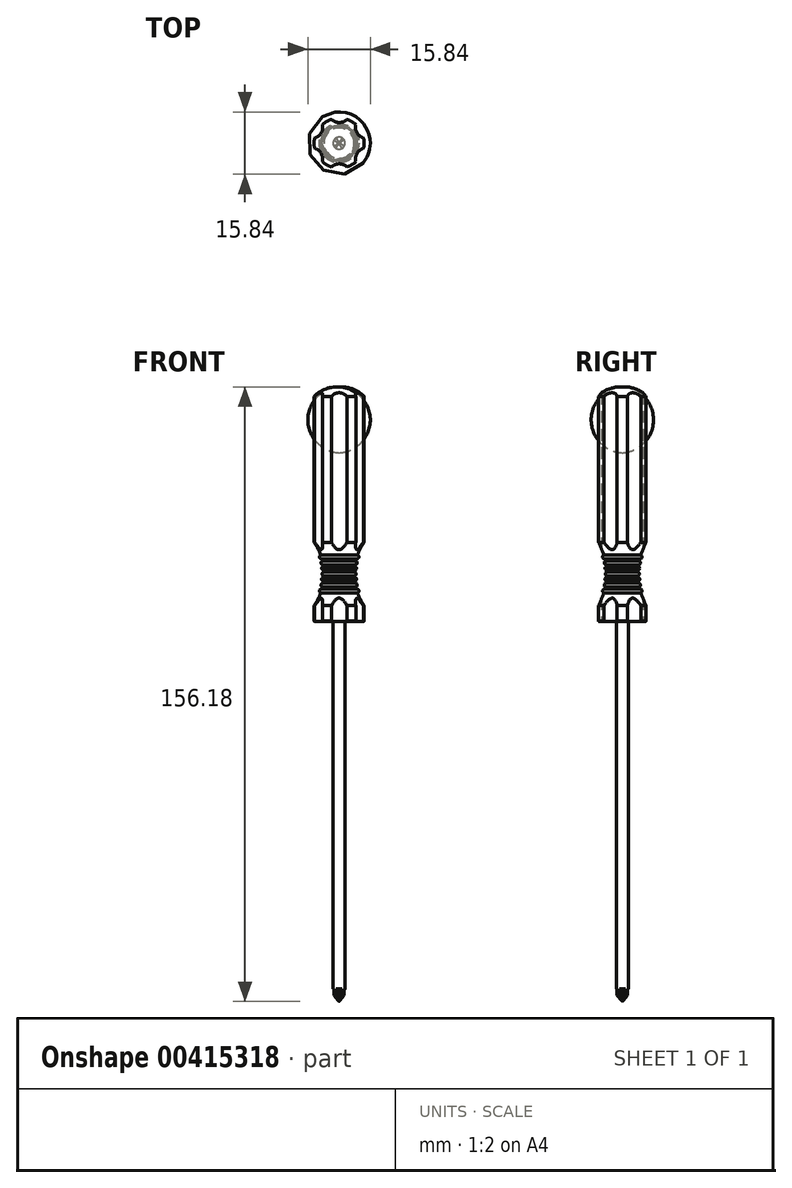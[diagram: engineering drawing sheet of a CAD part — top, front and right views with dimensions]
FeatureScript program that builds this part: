
annotation { "Feature Type Name" : "Feature", "Feature Type Description" : "" }
export const myFeature = defineFeature(function(context is Context, id is Id, definition is map)
    precondition{}
    {
        {
            var Q0;
            Q0=qCreatedBy(makeId("Front.planeOp"),FACE);
            var sketch = newSketch(context, id + "F0", { "sketchPlane" : qUnion([Q0])});
            skLineSegment(sketch, "E0", {"start": v(-6.35, 0) * mm, "end": v(-6.35, 57.15) * mm});
            skArc(sketch, "E1", {"start": v(0, 59.55) * mm, "mid": v(-3.43, 59.02) * mm, "end": v(-6.35, 57.15) * mm});
            skLineSegment(sketch, "E2", {"start": v(-6.35, 0) * mm, "end": v(-1.52, 0) * mm});
            skLineSegment(sketch, "E3", {"start": v(-1.52, 0) * mm, "end": v(-1.52, -95.1) * mm});
            skLineSegment(sketch, "E4", {"start": v(-1.52, -95.1) * mm, "end": v(0, -96.62) * mm});
            skLineSegment(sketch, "E5", {"start": v(0, -96.62) * mm, "end": v(0, 0) * mm});
            skPoint(sketch, "E6.end.orphan", {"position": v(0, 57.8) * mm});
            skLineSegment(sketch, "E7", {"start": v(0, 0) * mm, "end": v(0, 59.55) * mm});
            skSolve(sketch);
        }
        {
            var Q0;
            Q0 = qSketchRegion(id + "F0", true);
            var Q1;
            Q1=sQuery(id+"F0.wireOp",EDGE,"E7");
            revolve(context, id + "F1", {"entities" : qUnion([Q0]), "axis" : qUnion([Q1]), "revolveType" : RevolveType.FULL});
        }
        {
            var Q0;
            Q0=qCreatedBy(makeId("Front.planeOp"),FACE);
            var sketch = newSketch(context, id + "F2", { "sketchPlane" : qUnion([Q0])});
            skLineSegment(sketch, "E8", {"start": v(0, 0) * mm, "end": v(0, 87.28) * mm, "construction": true});
            skLineSegment(sketch, "E9", {"start": v(-6.93, 20.86) * mm, "end": v(-17.62, 12.03) * mm});
            skLineSegment(sketch, "E10", {"start": v(-17.62, 12.03) * mm, "end": v(-6.93, 3.2) * mm});
            skLineSegment(sketch, "E11", {"start": v(-6.93, 0.53) * mm, "end": v(-5.13, -0.97) * mm});
            skLineSegment(sketch, "E12", {"start": v(-5.13, -0.97) * mm, "end": v(-6.93, -0.97) * mm});
            skLineSegment(sketch, "E13", {"start": v(-6.93, -0.97) * mm, "end": v(-6.93, 0.53) * mm});
            skArc(sketch, "E14", {"start": v(-6.93, 3.2) * mm, "mid": v(-6.17, 4.25) * mm, "end": v(-5.51, 5.36) * mm});
            skArc(sketch, "E15", {"start": v(-4.67, 16.82) * mm, "mid": v(-5, 16.2) * mm, "end": v(-4.37, 15.89) * mm});
            skArc(sketch, "E16", {"start": v(-4.23, 15.33) * mm, "mid": v(-4.6, 14.76) * mm, "end": v(-4.03, 14.38) * mm});
            skArc(sketch, "E17.trimOffspring", {"start": v(-5.51, 18.7) * mm, "mid": v(-6.17, 19.82) * mm, "end": v(-6.93, 20.86) * mm});
            skArc(sketch, "E18.trimOffspring", {"start": v(-4.87, 17.34) * mm, "mid": v(-5.18, 18.03) * mm, "end": v(-5.51, 18.7) * mm});
            skArc(sketch, "E19.trimOffspring", {"start": v(-4.67, 16.82) * mm, "mid": v(-4.77, 17.08) * mm, "end": v(-4.87, 17.34) * mm});
            skArc(sketch, "E20.trimOffspring", {"start": v(-4.23, 15.33) * mm, "mid": v(-4.3, 15.61) * mm, "end": v(-4.37, 15.89) * mm});
            skLineSegment(sketch, "E21", {"start": v(-17.62, 12.03) * mm, "end": v(10.97, 12.03) * mm, "construction": true});
            skArc(sketch, "E22.MirrorCS", {"start": v(-4.67, 7.25) * mm, "mid": v(-4.77, 6.98) * mm, "end": v(-4.87, 6.72) * mm});
            skArc(sketch, "E23.MirrorCS", {"start": v(-4.23, 8.73) * mm, "mid": v(-4.3, 8.46) * mm, "end": v(-4.37, 8.18) * mm});
            skArc(sketch, "E24.MirrorCS", {"start": v(-5.27, 5.83) * mm, "mid": v(-5.4, 5.6) * mm, "end": v(-5.51, 5.36) * mm});
            skArc(sketch, "E25.MirrorCS", {"start": v(-4.67, 7.25) * mm, "mid": v(-5, 7.87) * mm, "end": v(-4.37, 8.18) * mm});
            skArc(sketch, "E26.MirrorCS", {"start": v(-4.23, 8.73) * mm, "mid": v(-4.6, 9.3) * mm, "end": v(-4.03, 9.7) * mm});
            skArc(sketch, "E27.trimOffspring", {"start": v(-4.03, 9.7) * mm, "mid": v(-4, 9.95) * mm, "end": v(-3.96, 10.2) * mm});
            skArc(sketch, "E28.trimOffspring", {"start": v(-4.37, 8.18) * mm, "mid": v(-4.3, 8.46) * mm, "end": v(-4.23, 8.73) * mm});
            skArc(sketch, "E29.trimOffspring", {"start": v(-4.87, 6.72) * mm, "mid": v(-4.77, 6.98) * mm, "end": v(-4.67, 7.25) * mm});
            skArc(sketch, "E30.trimOffspring", {"start": v(-5.51, 5.36) * mm, "mid": v(-5.18, 6.03) * mm, "end": v(-4.87, 6.72) * mm});
            skArc(sketch, "E31", {"start": v(-3.85, 12.52) * mm, "mid": v(-4.33, 12.03) * mm, "end": v(-3.85, 11.55) * mm});
            skArc(sketch, "E32", {"start": v(-3.87, 11.17) * mm, "mid": v(-4.43, 10.74) * mm, "end": v(-3.96, 10.2) * mm});
            skArc(sketch, "E33", {"start": v(-3.97, 13.96) * mm, "mid": v(-4.4, 13.42) * mm, "end": v(-3.87, 12.99) * mm});
            skArc(sketch, "E34.trimOffspring", {"start": v(-3.97, 13.96) * mm, "mid": v(-4, 14.17) * mm, "end": v(-4.03, 14.38) * mm});
            skArc(sketch, "E35.trimOffspring", {"start": v(-3.85, 12.52) * mm, "mid": v(-3.86, 12.75) * mm, "end": v(-3.87, 12.99) * mm});
            skArc(sketch, "E36.trimOffspring", {"start": v(-3.87, 11.17) * mm, "mid": v(-3.86, 11.36) * mm, "end": v(-3.85, 11.55) * mm});
            skPoint(sketch, "E37.orphan", {"position": v(-6, 19.55) * mm});
            skPoint(sketch, "E38.orphan", {"position": v(-5.27, 18.24) * mm});
            skSolve(sketch);
        }
        {
            var Q0;
            Q0 = qSketchRegion(id + "F2", true);
            var Q1;
            Q1=sQuery(id+"F2.wireOp",EDGE,"E8");
            revolve(context, id + "F3", {"operationType" : NewBodyOperationType.REMOVE, "entities" : qUnion([Q0]), "axis" : qUnion([Q1]), "revolveType" : RevolveType.FULL, "oppositeDirection" : true});
        }
        {
            var Q0;
            Q0=qCreatedBy(makeId("Top.planeOp"),FACE);
            var sketch = newSketch(context, id + "F4", { "sketchPlane" : qUnion([Q0])});
            skArc(sketch, "E39", {"start": v(-2, 6.04) * mm, "mid": v(0, 5.25) * mm, "end": v(2, 6.04) * mm});
            skLineSegment(sketch, "E40", {"start": v(-2, 6.04) * mm, "end": v(0, 8.15) * mm});
            skLineSegment(sketch, "E41", {"start": v(2, 6.04) * mm, "end": v(0, 8.15) * mm});
            skArc(sketch, "E42.1.0", {"start": v(-6.23, 1.3) * mm, "mid": v(-4.55, 2.63) * mm, "end": v(-4.24, 4.74) * mm});
            skLineSegment(sketch, "E42.1.1", {"start": v(-6.23, 1.3) * mm, "end": v(-7.06, 4.08) * mm});
            skLineSegment(sketch, "E42.1.2", {"start": v(-4.24, 4.74) * mm, "end": v(-7.06, 4.08) * mm});
            skArc(sketch, "E42.2.0", {"start": v(-4.24, -4.74) * mm, "mid": v(-4.55, -2.63) * mm, "end": v(-6.23, -1.3) * mm});
            skLineSegment(sketch, "E42.2.1", {"start": v(-4.24, -4.74) * mm, "end": v(-7.06, -4.08) * mm});
            skLineSegment(sketch, "E42.2.2", {"start": v(-6.23, -1.3) * mm, "end": v(-7.06, -4.08) * mm});
            skArc(sketch, "E42.3.0", {"start": v(2, -6.04) * mm, "mid": v(0, -5.25) * mm, "end": v(-2, -6.04) * mm});
            skLineSegment(sketch, "E42.3.1", {"start": v(2, -6.04) * mm, "end": v(0, -8.15) * mm});
            skLineSegment(sketch, "E42.3.2", {"start": v(-2, -6.04) * mm, "end": v(0, -8.15) * mm});
            skArc(sketch, "E42.4.0", {"start": v(6.23, -1.3) * mm, "mid": v(4.55, -2.63) * mm, "end": v(4.24, -4.74) * mm});
            skLineSegment(sketch, "E42.4.1", {"start": v(6.23, -1.3) * mm, "end": v(7.06, -4.08) * mm});
            skLineSegment(sketch, "E42.4.2", {"start": v(4.24, -4.74) * mm, "end": v(7.06, -4.08) * mm});
            skArc(sketch, "E42.5.0", {"start": v(4.24, 4.74) * mm, "mid": v(4.55, 2.63) * mm, "end": v(6.23, 1.3) * mm});
            skLineSegment(sketch, "E42.5.1", {"start": v(4.24, 4.74) * mm, "end": v(7.06, 4.08) * mm});
            skLineSegment(sketch, "E42.5.2", {"start": v(6.23, 1.3) * mm, "end": v(7.06, 4.08) * mm});
            skPoint(sketch, "E42.center", {"position": v(0, 0) * mm});
            skSolve(sketch);
        }
        {
            var Q0;
            Q0 = qSketchRegion(id + "F4", true);
            extrude(context, id + "F5", {"entities" : qUnion([Q0]), "operationType" : NewBodyOperationType.REMOVE, "endBound" : BoundingType.THROUGH_ALL, "depth" : 25.4 * mm});
        }
        {
            var Q0;
            Q0=qCreatedBy(makeId("Top.planeOp"),FACE);
            cPlane(context, id + "F6", {"entities" : qUnion([Q0]), "cplaneType" : CPlaneType.OFFSET, "offset" : 96.57 * mm, "oppositeDirection" : true, "width" : 152.4 * mm, "height" : 152.4 * mm});
        }
        {
            var Q0;
            Q0=qCreatedBy(id+"F6.planeOp",FACE);
            var sketch = newSketch(context, id + "F7", { "sketchPlane" : qUnion([Q0])});
            skLineSegment(sketch, "E43", {"start": v(-0.14, -0.23) * mm, "end": v(-0.89, -1.48) * mm});
            skLineSegment(sketch, "E44", {"start": v(-0.89, -1.48) * mm, "end": v(0, -2.01) * mm, "construction": true});
            skLineSegment(sketch, "E45", {"start": v(0, -2.01) * mm, "end": v(0, 2.15) * mm, "construction": true});
            skLineSegment(sketch, "E46.MirrorCS", {"start": v(0.14, -0.23) * mm, "end": v(0.89, -1.48) * mm});
            skArc(sketch, "E47", {"start": v(-0.89, -1.48) * mm, "mid": v(0, -1.72) * mm, "end": v(0.89, -1.48) * mm});
            skLineSegment(sketch, "E48", {"start": v(-0.14, -0.23) * mm, "end": v(0.14, -0.23) * mm, "construction": true});
            skArc(sketch, "E49", {"start": v(0.14, -0.24) * mm, "mid": v(0, -0.15) * mm, "end": v(-0.14, -0.24) * mm});
            skPoint(sketch, "E49.third.point", {"position": v(0, -0.48) * mm});
            skLineSegment(sketch, "E50.1.0", {"start": v(0.23, -0.14) * mm, "end": v(1.48, -0.89) * mm});
            skArc(sketch, "E50.1.1", {"start": v(1.48, -0.89) * mm, "mid": v(1.72, 0) * mm, "end": v(1.48, 0.89) * mm});
            skLineSegment(sketch, "E50.1.2", {"start": v(0.23, 0.14) * mm, "end": v(1.48, 0.89) * mm});
            skPoint(sketch, "E50.1.3", {"position": v(0.48, 0) * mm});
            skLineSegment(sketch, "E50.1.6", {"start": v(0.23, -0.14) * mm, "end": v(0.23, 0.14) * mm, "construction": true});
            skArc(sketch, "E50.1.7", {"start": v(0.24, 0.14) * mm, "mid": v(0.15, 0) * mm, "end": v(0.24, -0.14) * mm});
            skLineSegment(sketch, "E50.2.0", {"start": v(0.14, 0.23) * mm, "end": v(0.89, 1.48) * mm});
            skArc(sketch, "E50.2.1", {"start": v(0.89, 1.48) * mm, "mid": v(0, 1.72) * mm, "end": v(-0.89, 1.48) * mm});
            skLineSegment(sketch, "E50.2.2", {"start": v(-0.14, 0.23) * mm, "end": v(-0.89, 1.48) * mm});
            skPoint(sketch, "E50.2.3", {"position": v(0, 0.48) * mm});
            skLineSegment(sketch, "E50.2.6", {"start": v(0.14, 0.23) * mm, "end": v(-0.14, 0.23) * mm, "construction": true});
            skArc(sketch, "E50.2.7", {"start": v(-0.14, 0.24) * mm, "mid": v(0, 0.15) * mm, "end": v(0.14, 0.24) * mm});
            skLineSegment(sketch, "E50.3.0", {"start": v(-0.23, 0.14) * mm, "end": v(-1.48, 0.89) * mm});
            skArc(sketch, "E50.3.1", {"start": v(-1.48, 0.89) * mm, "mid": v(-1.72, 0) * mm, "end": v(-1.48, -0.89) * mm});
            skLineSegment(sketch, "E50.3.2", {"start": v(-0.23, -0.14) * mm, "end": v(-1.48, -0.89) * mm});
            skPoint(sketch, "E50.3.3", {"position": v(-0.48, 0) * mm});
            skLineSegment(sketch, "E50.3.6", {"start": v(-0.23, 0.14) * mm, "end": v(-0.23, -0.14) * mm, "construction": true});
            skArc(sketch, "E50.3.7", {"start": v(-0.24, -0.14) * mm, "mid": v(-0.15, 0) * mm, "end": v(-0.24, 0.14) * mm});
            skSolve(sketch);
        }
        {
            var Q0;
            Q0 = qSketchRegion(id + "F7", true);
            extrude(context, id + "F8", {"entities" : qUnion([Q0]), "operationType" : NewBodyOperationType.REMOVE, "depth" : 3.17 * mm});
        }
    });
